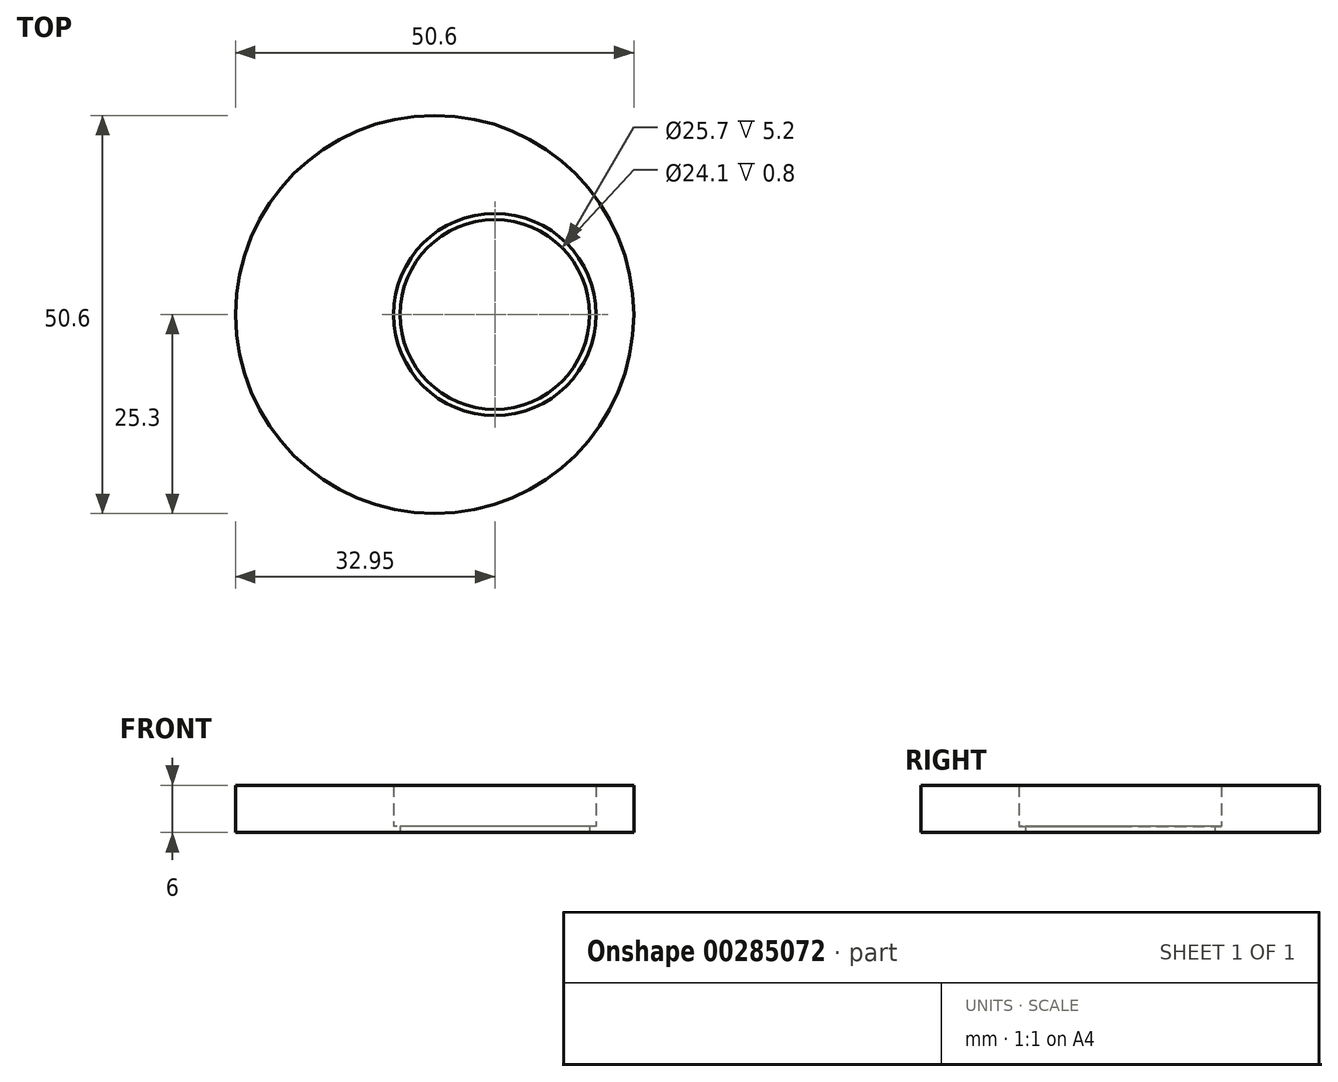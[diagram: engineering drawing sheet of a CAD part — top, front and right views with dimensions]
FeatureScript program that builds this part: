
annotation { "Feature Type Name" : "Feature", "Feature Type Description" : "" }
export const myFeature = defineFeature(function(context is Context, id is Id, definition is map)
    precondition{}
    {
        {
            var Q0;
            Q0=qCreatedBy(makeId("Top.planeOp"),FACE);
            var sketch = newSketch(context, id + "F0", { "sketchPlane" : qUnion([Q0])});
            skCircle(sketch, "E0", {"center": v(0, 0) * mm, "radius": 25.3 * mm});
            skLineSegment(sketch, "E1", {"start": v(0, 0) * mm, "end": v(25.3, 0) * mm, "construction": true});
            skPoint(sketch, "E2", {"position": v(12.65, 0) * mm});
            skPoint(sketch, "E3", {"position": v(7.65, 0) * mm});
            skCircle(sketch, "E4", {"center": v(7.65, 0) * mm, "radius": 12.85 * mm});
            skCircle(sketch, "E5", {"center": v(7.65, 0) * mm, "radius": 12.05 * mm});
            skSolve(sketch);
        }
        {
            var Q0;
            Q0=makeQuery(id+"F0.imprint","IMPRINT",FACE,{"disambiguationData":[TD([[makeQuery(id+"F0.imprint","IMPRINT",EDGE,{"derivedFrom":sQuery(id+"F0.wireOp",EDGE,"E0")}),1.0]])]});
            extrude(context, id + "F1", {"entities" : qUnion([Q0]), "depth" : 6 * mm});
        }
        {
            var Q0;
            Q0=makeQuery(id+"F0.imprint","IMPRINT",FACE,{"disambiguationData":[TD([[makeQuery(id+"F0.imprint","IMPRINT",EDGE,{"derivedFrom":sQuery(id+"F0.wireOp",EDGE,"E4")}),1.0]])]});
            extrude(context, id + "F2", {"entities" : qUnion([Q0]), "operationType" : NewBodyOperationType.ADD, "depth" : 0.8 * mm});
        }
    });
